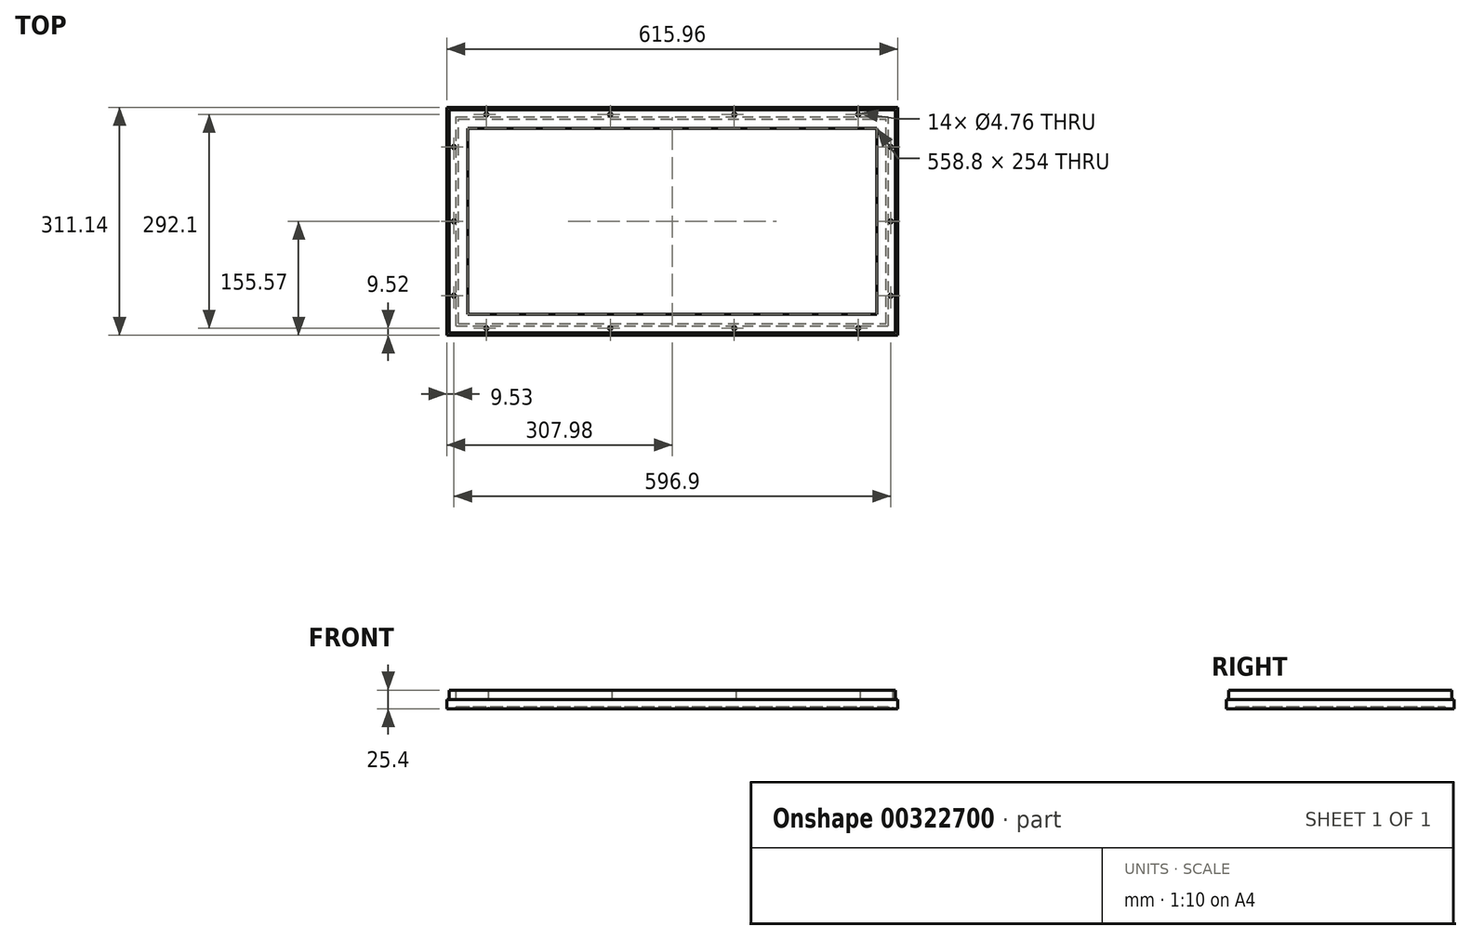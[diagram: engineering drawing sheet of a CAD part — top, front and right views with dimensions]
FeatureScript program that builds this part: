
annotation { "Feature Type Name" : "Feature", "Feature Type Description" : "" }
export const myFeature = defineFeature(function(context is Context, id is Id, definition is map)
    precondition{}
    {
        {
            var Q0;
            Q0=qCreatedBy(makeId("Top.planeOp"),FACE);
            var sketch = newSketch(context, id + "F0", { "sketchPlane" : qUnion([Q0])});
            skLineSegment(sketch, "E0.bottom", {"start": v(-304.8, -152.4) * mm, "end": v(304.8, -152.4) * mm});
            skLineSegment(sketch, "E0.top", {"start": v(-304.8, 152.4) * mm, "end": v(304.8, 152.4) * mm});
            skLineSegment(sketch, "E0.left", {"start": v(-304.8, -152.4) * mm, "end": v(-304.8, 152.4) * mm});
            skLineSegment(sketch, "E0.right", {"start": v(304.8, -152.4) * mm, "end": v(304.8, 152.4) * mm});
            skPoint(sketch, "E0.middle", {"position": v(0, 0) * mm});
            skLineSegment(sketch, "E1.0", {"start": v(-279.4, -127) * mm, "end": v(-279.4, 127) * mm});
            skLineSegment(sketch, "E1.1", {"start": v(-279.4, -127) * mm, "end": v(279.4, -127) * mm});
            skLineSegment(sketch, "E1.2", {"start": v(279.4, -127) * mm, "end": v(279.4, 127) * mm});
            skLineSegment(sketch, "E1.3", {"start": v(-279.4, 127) * mm, "end": v(279.4, 127) * mm});
            skSolve(sketch);
        }
        {
            var Q0;
            Q0 = qSketchRegion(id + "F0", true);
            extrude(context, id + "F1", {"entities" : qUnion([Q0]), "depth" : 25.4 * mm});
        }
        {
            var Q0;
            Q0=qCreatedBy(makeId("Top.planeOp"),FACE);
            var sketch = newSketch(context, id + "F2", { "sketchPlane" : qUnion([Q0])});
            skPoint(sketch, "E2.middle", {"position": v(0, 0) * mm});
            skLineSegment(sketch, "E3.0", {"start": v(-304.8, -152.4) * mm, "end": v(304.8, -152.4) * mm});
            skLineSegment(sketch, "E3.1", {"start": v(-304.8, -152.4) * mm, "end": v(-304.8, 152.4) * mm});
            skLineSegment(sketch, "E3.2", {"start": v(-304.8, 152.4) * mm, "end": v(304.8, 152.4) * mm});
            skLineSegment(sketch, "E3.3", {"start": v(304.8, -152.4) * mm, "end": v(304.8, 152.4) * mm});
            skLineSegment(sketch, "E4.0", {"start": v(-292.1, -139.7) * mm, "end": v(292.1, -139.7) * mm});
            skLineSegment(sketch, "E4.1", {"start": v(-292.1, -139.7) * mm, "end": v(-292.1, 139.7) * mm});
            skLineSegment(sketch, "E4.2", {"start": v(-292.1, 139.7) * mm, "end": v(292.1, 139.7) * mm});
            skLineSegment(sketch, "E4.3", {"start": v(292.1, -139.7) * mm, "end": v(292.1, 139.7) * mm});
            skSolve(sketch);
        }
        {
            var Q0;
            Q0 = qSketchRegion(id + "F2", true);
            extrude(context, id + "F3", {"entities" : qUnion([Q0]), "operationType" : NewBodyOperationType.REMOVE, "depth" : 3.17 * mm});
        }
        {
            var Q0;
            Q0=qCreatedBy(makeId("Top.planeOp"),FACE);
            var sketch = newSketch(context, id + "F4", { "sketchPlane" : qUnion([Q0])});
            skLineSegment(sketch, "E5.0", {"start": v(-307.97, -155.58) * mm, "end": v(307.98, -155.58) * mm});
            skLineSegment(sketch, "E5.1", {"start": v(-307.97, -155.58) * mm, "end": v(-307.98, 155.58) * mm});
            skLineSegment(sketch, "E5.2", {"start": v(-307.98, 155.58) * mm, "end": v(307.97, 155.58) * mm});
            skLineSegment(sketch, "E5.3", {"start": v(307.98, -155.58) * mm, "end": v(307.97, 155.58) * mm});
            skLineSegment(sketch, "E6.0", {"start": v(-295.28, -142.88) * mm, "end": v(295.27, -142.88) * mm});
            skLineSegment(sketch, "E6.1", {"start": v(-295.28, -142.88) * mm, "end": v(-295.28, 142.88) * mm});
            skLineSegment(sketch, "E6.2", {"start": v(-295.28, 142.88) * mm, "end": v(295.27, 142.88) * mm});
            skLineSegment(sketch, "E6.3", {"start": v(295.27, -142.88) * mm, "end": v(295.27, 142.88) * mm});
            skSolve(sketch);
        }
        {
            var Q0;
            Q0 = qSketchRegion(id + "F4", true);
            extrude(context, id + "F5", {"entities" : qUnion([Q0]), "depth" : 3.17 * mm});
        }
        {
            var Q0;
            Q0=makeQuery(id+"F5.opExtrude","CAP_FACE",FACE,{"disambiguationData":[OSD([sQuery(id+"F4.wireOp",EDGE,"E5.0"),sQuery(id+"F4.wireOp",EDGE,"E5.1"),sQuery(id+"F4.wireOp",EDGE,"E5.2"),sQuery(id+"F4.wireOp",EDGE,"E5.3"),sQuery(id+"F4.wireOp",EDGE,"E6.0"),sQuery(id+"F4.wireOp",EDGE,"E6.1"),sQuery(id+"F4.wireOp",EDGE,"E6.2"),sQuery(id+"F4.wireOp",EDGE,"E6.3")])],"isStart":false});
            var sketch = newSketch(context, id + "F6", { "sketchPlane" : qUnion([Q0])});
            skLineSegment(sketch, "E7.0", {"start": v(-307.98, 155.58) * mm, "end": v(307.97, 155.58) * mm});
            skLineSegment(sketch, "E7.1", {"start": v(-304.8, 152.4) * mm, "end": v(304.8, 152.4) * mm});
            skLineSegment(sketch, "E7.2", {"start": v(-307.97, -155.58) * mm, "end": v(-307.98, 155.58) * mm});
            skLineSegment(sketch, "E7.3", {"start": v(-304.8, -152.4) * mm, "end": v(-304.8, 152.4) * mm});
            skLineSegment(sketch, "E7.4", {"start": v(-304.8, -152.4) * mm, "end": v(304.8, -152.4) * mm});
            skLineSegment(sketch, "E7.5", {"start": v(-307.97, -155.58) * mm, "end": v(307.98, -155.58) * mm});
            skLineSegment(sketch, "E7.6", {"start": v(307.98, -155.58) * mm, "end": v(307.97, 155.58) * mm});
            skLineSegment(sketch, "E7.7", {"start": v(304.8, -152.4) * mm, "end": v(304.8, 152.4) * mm});
            skSolve(sketch);
        }
        {
            var Q0;
            Q0 = qSketchRegion(id + "F6", true);
            extrude(context, id + "F7", {"entities" : qUnion([Q0]), "operationType" : NewBodyOperationType.ADD, "depth" : 9.52 * mm});
        }
        {
            var Q0;
            Q0=qCreatedBy(makeId("Top.planeOp"),FACE);
            var sketch = newSketch(context, id + "F8", { "sketchPlane" : qUnion([Q0])});
            skPoint(sketch, "E8.middle", {"position": v(0, 0) * mm});
            skCircle(sketch, "E9", {"center": v(-254, 146.05) * mm, "radius": 2.38 * mm});
            skCircle(sketch, "E10", {"center": v(-84.67, 146.05) * mm, "radius": 2.38 * mm});
            skCircle(sketch, "E11", {"center": v(84.67, 146.05) * mm, "radius": 2.38 * mm});
            skCircle(sketch, "E12", {"center": v(254, 146.05) * mm, "radius": 2.38 * mm});
            skCircle(sketch, "E13", {"center": v(298.45, 101.6) * mm, "radius": 2.38 * mm});
            skCircle(sketch, "E14", {"center": v(298.45, 0) * mm, "radius": 2.38 * mm});
            skCircle(sketch, "E15", {"center": v(298.45, -101.6) * mm, "radius": 2.38 * mm});
            skCircle(sketch, "E16", {"center": v(254, -146.05) * mm, "radius": 2.38 * mm});
            skCircle(sketch, "E17", {"center": v(84.67, -146.05) * mm, "radius": 2.38 * mm});
            skCircle(sketch, "E18", {"center": v(-84.67, -146.05) * mm, "radius": 2.38 * mm});
            skCircle(sketch, "E19", {"center": v(-254, -146.05) * mm, "radius": 2.38 * mm});
            skCircle(sketch, "E20", {"center": v(-298.45, 101.6) * mm, "radius": 2.38 * mm});
            skCircle(sketch, "E21", {"center": v(-298.45, 0) * mm, "radius": 2.38 * mm});
            skCircle(sketch, "E22", {"center": v(-298.45, -101.6) * mm, "radius": 2.38 * mm});
            skLineSegment(sketch, "E23", {"start": v(-298.45, 101.6) * mm, "end": v(-298.45, 0) * mm, "construction": true});
            skLineSegment(sketch, "E24", {"start": v(-298.45, 0) * mm, "end": v(-298.45, -101.6) * mm, "construction": true});
            skLineSegment(sketch, "E25", {"start": v(-254, 146.05) * mm, "end": v(-84.67, 146.05) * mm, "construction": true});
            skLineSegment(sketch, "E26", {"start": v(84.67, 146.05) * mm, "end": v(-84.67, 146.05) * mm, "construction": true});
            skLineSegment(sketch, "E27", {"start": v(84.67, 146.05) * mm, "end": v(254, 146.05) * mm, "construction": true});
            skLineSegment(sketch, "E28", {"start": v(298.45, 101.6) * mm, "end": v(298.45, 0) * mm, "construction": true});
            skLineSegment(sketch, "E29", {"start": v(298.45, 0) * mm, "end": v(298.45, -101.6) * mm, "construction": true});
            skLineSegment(sketch, "E30", {"start": v(254, -146.05) * mm, "end": v(84.67, -146.05) * mm, "construction": true});
            skLineSegment(sketch, "E31", {"start": v(84.67, -146.05) * mm, "end": v(-84.67, -146.05) * mm, "construction": true});
            skLineSegment(sketch, "E32", {"start": v(-84.67, -146.05) * mm, "end": v(-254, -146.05) * mm, "construction": true});
            skLineSegment(sketch, "E33", {"start": v(0, 146.05) * mm, "end": v(0, -146.05) * mm, "construction": true});
            skLineSegment(sketch, "E34", {"start": v(-298.45, 0) * mm, "end": v(298.45, 0) * mm, "construction": true});
            skLineSegment(sketch, "E35", {"start": v(-298.45, 101.6) * mm, "end": v(-298.45, 146.05) * mm, "construction": true});
            skLineSegment(sketch, "E36", {"start": v(-298.45, 146.05) * mm, "end": v(-254, 146.05) * mm, "construction": true});
            skLineSegment(sketch, "E37", {"start": v(298.45, -101.6) * mm, "end": v(298.45, -146.05) * mm, "construction": true});
            skLineSegment(sketch, "E38", {"start": v(298.45, -146.05) * mm, "end": v(254, -146.05) * mm, "construction": true});
            skSolve(sketch);
        }
        {
            var Q0;
            Q0 = qSketchRegion(id + "F8", true);
            extrude(context, id + "F9", {"entities" : qUnion([Q0]), "operationType" : NewBodyOperationType.REMOVE, "endBound" : BoundingType.THROUGH_ALL, "depth" : 25.4 * mm});
        }
    });
